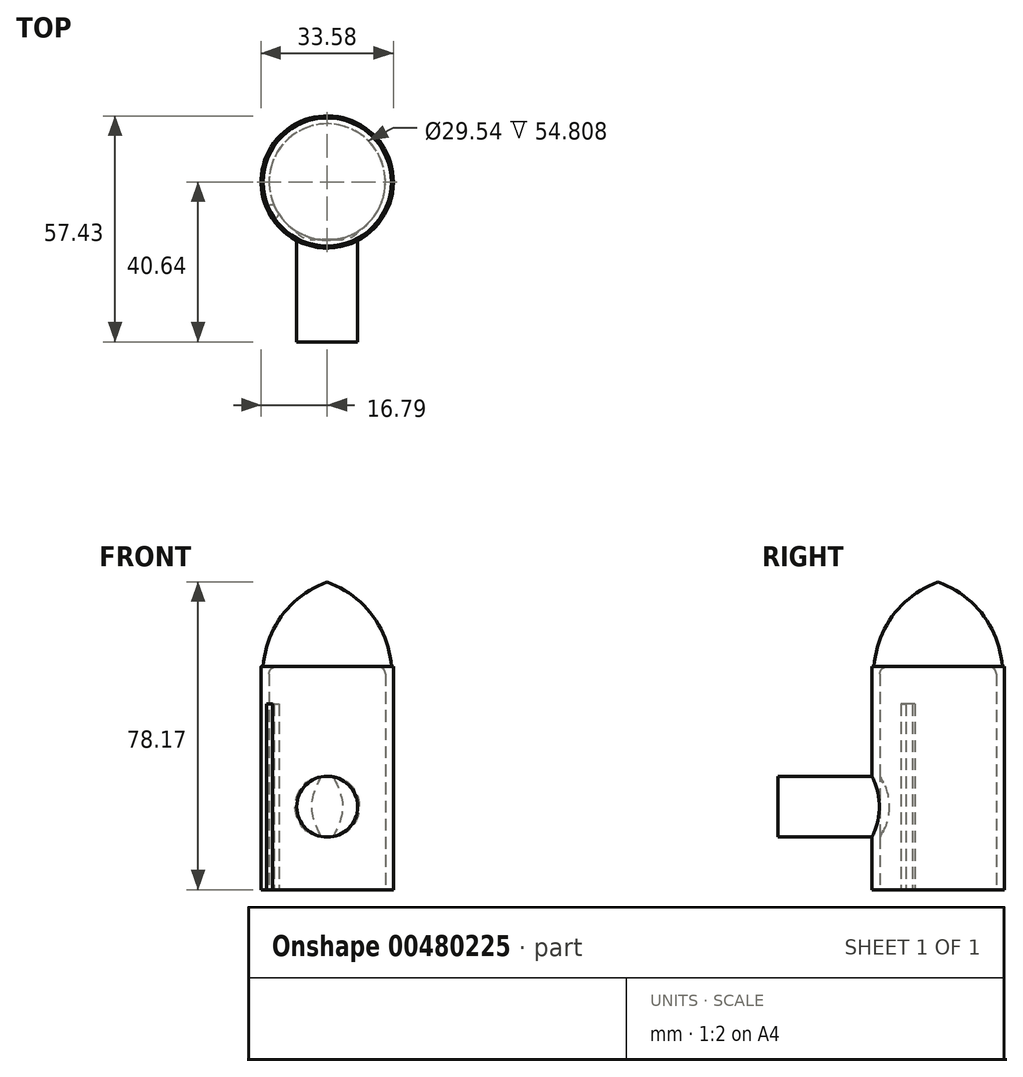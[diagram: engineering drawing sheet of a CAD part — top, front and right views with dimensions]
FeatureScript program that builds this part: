
annotation { "Feature Type Name" : "Feature", "Feature Type Description" : "" }
export const myFeature = defineFeature(function(context is Context, id is Id, definition is map)
    precondition{}
    {
        {
            var Q0;
            Q0=qCreatedBy(makeId("Top.planeOp"),FACE);
            var sketch = newSketch(context, id + "F0", { "sketchPlane" : qUnion([Q0])});
            skCircle(sketch, "E0", {"center": v(0, 0) * mm, "radius": 14.77 * mm});
            skCircle(sketch, "E1", {"center": v(0, 0) * mm, "radius": 16.79 * mm});
            skSolve(sketch);
        }
        {
            var Q0;
            Q0 = qSketchRegion(id + "F0", true);
            extrude(context, id + "F1", {"entities" : qUnion([Q0]), "depth" : 44.07 * mm});
        }
        {
            var Q0;
            Q0=qCreatedBy(makeId("Front.planeOp"),FACE);
            var sketch = newSketch(context, id + "F2", { "sketchPlane" : qUnion([Q0])});
            skCircle(sketch, "E2", {"center": v(0, 8.38) * mm, "radius": 7.73 * mm});
            skSolve(sketch);
        }
        {
            var Q0;
            Q0 = qSketchRegion(id + "F2", true);
            var Q1;
            Q1 = qSketchRegion(id + "F11", true);
            extrude(context, id + "F3", {"entities" : qUnion([Q0, Q1]), "operationType" : NewBodyOperationType.ADD, "depth" : 27.94 * mm, "offsetDistance" : 25.4 * mm});
        }
        {
            var Q0;
            Q0=makeQuery(id+"F3.opExtrude","CAP_FACE",FACE,{"disambiguationData":[OSD([sQuery(id+"F2.wireOp",EDGE,"E2")])],"isStart":true});
            var sketch = newSketch(context, id + "F4", { "sketchPlane" : qUnion([Q0])});
            skCircle(sketch, "E3", {"center": v(0, 8.38) * mm, "radius": 8.13 * mm});
            skSolve(sketch);
        }
        {
            var Q0;
            Q0 = qSketchRegion(id + "F4", true);
            extrude(context, id + "F5", {"entities" : qUnion([Q0]), "operationType" : NewBodyOperationType.REMOVE, "oppositeDirection" : true, "depth" : 13.97 * mm});
        }
        {
            var Q0;
            Q0=qCreatedBy(makeId("Right.planeOp"),FACE);
            var sketch = newSketch(context, id + "F6", { "sketchPlane" : qUnion([Q0])});
            skLineSegment(sketch, "E4", {"start": v(16.3, 43.95) * mm, "end": v(-16.28, 43.95) * mm});
            skLineSegment(sketch, "E5", {"start": v(0, 65.47) * mm, "end": v(0, 43.95) * mm});
            skArc(sketch, "E6", {"start": v(0, 65.47) * mm, "mid": v(-11.35, 57.14) * mm, "end": v(-16.28, 43.95) * mm});
            skSolve(sketch);
        }
        {
            var Q0;
            Q0 = qSketchRegion(id + "F6", true);
            var Q1;
            Q1=sQuery(id+"F6.wireOp",EDGE,"E5");
            revolve(context, id + "F7", {"operationType" : NewBodyOperationType.ADD, "entities" : qUnion([Q0]), "axis" : qUnion([Q1]), "revolveType" : RevolveType.FULL});
        }
        {
            var Q0;
            Q0=makeQuery(id+"F5.boolean.opBoolean","COPY",FACE,{"derivedFrom":makeQuery(id+"F5.opExtrude","CAP_FACE",FACE,{"disambiguationData":[OSD([sQuery(id+"F4.wireOp",EDGE,"E3")])],"isStart":false})});
            extrude(context, id + "F8", {"entities" : qUnion([Q0]), "operationType" : NewBodyOperationType.REMOVE, "oppositeDirection" : true, "depth" : 0.66 * mm});
        }
        {
            var Q0;
            {var subQ0=sQuery(id+"F4.wireOp",EDGE,"E3");Q0=makeQuery(id+"F8.boolean.opBoolean","COPY",EDGE,{"derivedFrom":makeQuery(id+"F8.opExtrude","CAP_EDGE",EDGE,{"disambiguationData":[OSD([subQ0]),TDD([makeQuery(id+"F5.boolean.opBoolean","COPY",EDGE,{"disambiguationData":[OD(1.0)],"derivedFrom":makeQuery(id+"F5.opExtrude","CAP_EDGE",EDGE,{"disambiguationData":[OSD([subQ0])],"isStart":false})})])],"isStart":false})});}
            var Q1;
            {var subQ0=sQuery(id+"F4.wireOp",EDGE,"E3");Q1=makeQuery(id+"F8.boolean.opBoolean","COPY",EDGE,{"derivedFrom":makeQuery(id+"F8.opExtrude","CAP_EDGE",EDGE,{"disambiguationData":[OSD([subQ0]),TDD([makeQuery(id+"F5.boolean.opBoolean","COPY",EDGE,{"disambiguationData":[OD(0.0)],"derivedFrom":makeQuery(id+"F5.opExtrude","CAP_EDGE",EDGE,{"disambiguationData":[OSD([subQ0])],"isStart":false})})])],"isStart":false})});}
            fillet(context, id + "F9", {"entities" : qUnion([Q0, Q1]), "radius" : 5.08 * mm, "tangentPropagation" : true, "allowEdgeOverflow" : false});
        }
        {
            var Q0;
            Q0=makeQuery(id+"F7.boolean.opBoolean","INTERSECT",EDGE,{"derivedFrom":[makeQuery(id+"F1.opExtrude","SWEPT_FACE",FACE,{"disambiguationData":[OSD([sQuery(id+"F0.wireOp",EDGE,"E0")])]}),makeQuery(id+"F7.opRevolve","SWEPT_FACE",FACE,{"disambiguationData":[OSD([sQuery(id+"F6.wireOp",EDGE,"E4")])]})]});
            fillet(context, id + "F10", {"entities" : qUnion([Q0]), "radius" : 1.84 * mm, "tangentPropagation" : true, "allowEdgeOverflow" : false});
        }
        {
            var Q0;
            Q0=qCreatedBy(makeId("Top.planeOp"),FACE);
            var sketch = newSketch(context, id + "F11", { "sketchPlane" : qUnion([Q0])});
            skCircle(sketch, "E7", {"center": v(-14, -7.66) * mm, "radius": 1.8 * mm});
            skSolve(sketch);
        }
        {
            var Q0;
            Q0 = qSketchRegion(id + "F11", true);
            extrude(context, id + "F12", {"entities" : qUnion([Q0]), "operationType" : NewBodyOperationType.REMOVE, "depth" : 34.47 * mm});
        }
        {
            var Q0;
            Q0=makeQuery(id+"F1.opExtrude","CAP_FACE",FACE,{"disambiguationData":[OSD([sQuery(id+"F0.wireOp",EDGE,"E0"),sQuery(id+"F0.wireOp",EDGE,"E1")])],"isStart":true});
            extrude(context, id + "F13", {"entities" : qUnion([Q0]), "operationType" : NewBodyOperationType.ADD, "depth" : 12.7 * mm, "offsetDistance" : 25.4 * mm});
        }
        {
            var Q0;
            Q0=makeQuery(id+"F3.opExtrude","CAP_FACE",FACE,{"disambiguationData":[OSD([sQuery(id+"F2.wireOp",EDGE,"E2")])],"isStart":false});
            extrude(context, id + "F14", {"entities" : qUnion([Q0]), "operationType" : NewBodyOperationType.ADD, "depth" : 12.7 * mm, "offsetDistance" : 25.4 * mm});
        }
    });
